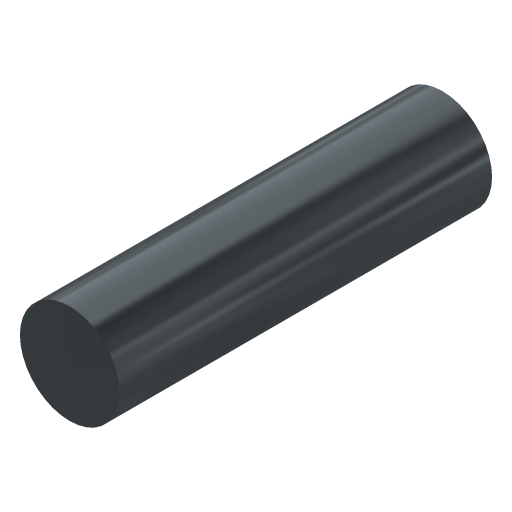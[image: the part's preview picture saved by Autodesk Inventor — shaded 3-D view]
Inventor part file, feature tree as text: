
AUTODESK INVENTOR PART (.ipt)
format: ipt  version: 2024 (Build 280153000, 153)  size: 121,856 bytes
history: native  units: in
note: dims shown in document units (in); Inventor stores cm internally (conversion verified against a paired STEP export)
features: extrude x1, sketch x1
ambient origin geometry x8: Origin, YZ Plane, XZ Plane, XY Plane, X Axis, Y Axis, Z Axis, Center Point
bodies: Solid1 (feature_tree)
feature tree (2):
  extrude  "Extrusion1"  Depth=1.1811in TaperAngle=0.0deg
  sketch  "Sketch1"  dims[d0=0.315in d1=1.1811in d2=0.0in]
